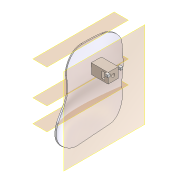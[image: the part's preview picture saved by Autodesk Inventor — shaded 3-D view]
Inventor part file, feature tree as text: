
AUTODESK INVENTOR PART (.ipt)
format: ipt  version: 2020.2 (Build 242310000, 310)  size: 382,464 bytes
history: native  units: mm
features: sketch x9, plane x5, extrude x5, loft x1, fillet x1
ambient origin geometry x8: Origin, YZ Plane, XZ Plane, XY Plane, X Axis, Y Axis, Z Axis, Center Point
bodies: Solid1 (feature_tree)
feature tree (21):
  sketch  "Sketch1"  dims[d0=1.0mm d1=20.0mm d2=1.0mm]
  plane  "Work Plane1"
  sketch  "Sketch2"  dims[d3=20.0mm d4=1.0mm]
  plane  "Work Plane2"
  sketch  "Sketch3"  dims[d5=30.0mm d6=1.0mm]
  plane  "Work Plane3"
  loft  "Loft1"
  fillet  "Fillet1"  Radius=1.0mm
  plane  "Work Plane4"
  extrude  "Extrusion1"  Depth=1.0mm
  extrude  "Extrusion2"  Depth=1.0mm
  extrude  "Extrusion3"  TaperAngle=0.0deg  [1 undecoded]
  extrude  "Extrusion4"  Depth=10.0mm TaperAngle=90.0deg
  plane  "Work Plane6"
  extrude  "Extrusion5"  Depth=15.0mm
  sketch  "Sketch4"  dims[d7=0.0mm d8=90.0deg d9=0.0mm d10=90.0deg]
  sketch  "Sketch5"  dims[d11=0.0mm d12=90.0deg d13=10.0mm d14=90.0deg]
  sketch  "Sketch6"  dims[d15=15.0mm d16=15.0mm]
  sketch  "Sketch7"  dims[d17=9.0mm]
  sketch  "Sketch8"  dims[d18=9.0mm]
  sketch  "Sketch9"  dims[d19=3.0mm d20=0.0mm d21=0.0mm d23=3.0mm d24=3.0mm d25=2.5mm d26=6.0mm d27=10.0mm d28=0.0mm d29=0.2mm d30=2.0mm d31=2.0mm d32=3.0mm d33=0.2mm d34=2.0mm d35=2.0mm d36=3.0mm d37=2.0mm d38=0.0mm d39=3.0mm d40=2.0mm d41=0.0mm d42=-12.0mm d43=6.0mm d44=10.0mm d45=0.0mm]
note: 1 required parameter value undecoded (feature->parameter linkage not recoverable at this tier; creation-order binding heuristic only, values carry confidence <= 0.55)
